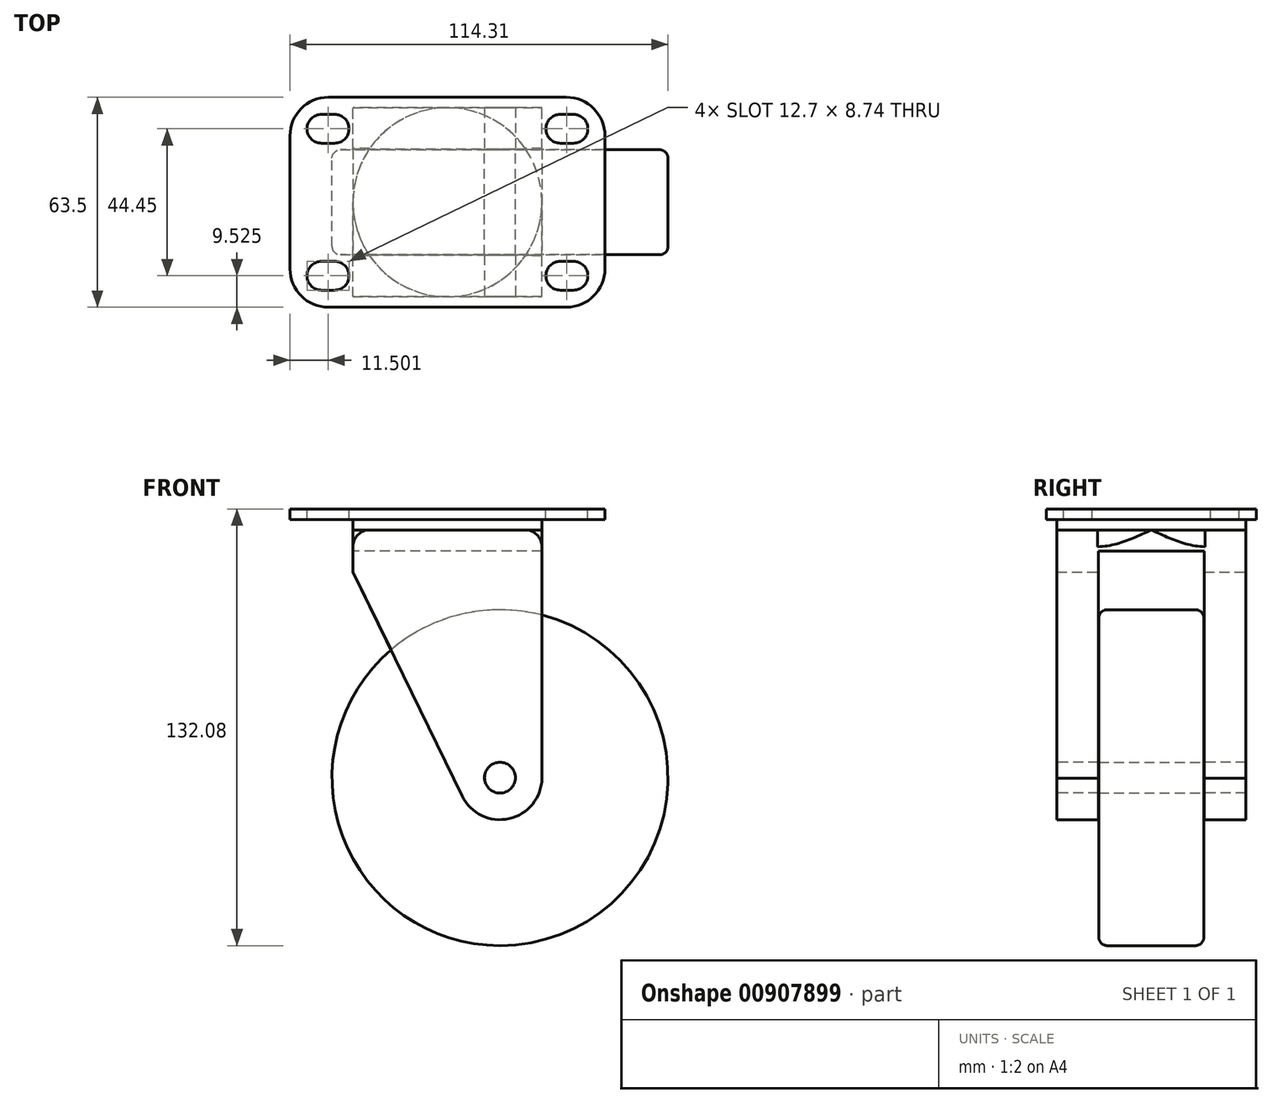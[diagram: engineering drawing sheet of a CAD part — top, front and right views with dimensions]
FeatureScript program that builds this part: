
annotation { "Feature Type Name" : "Feature", "Feature Type Description" : "" }
export const myFeature = defineFeature(function(context is Context, id is Id, definition is map)
    precondition{}
    {
        {
            var Q0;
            Q0=qCreatedBy(makeId("Top.planeOp"),FACE);
            var sketch = newSketch(context, id + "F0", { "sketchPlane" : qUnion([Q0])});
            skLineSegment(sketch, "E0.bottom", {"start": v(-47.62, 31.75) * mm, "end": v(47.63, 31.75) * mm});
            skLineSegment(sketch, "E0.top", {"start": v(-47.62, -31.75) * mm, "end": v(47.63, -31.75) * mm});
            skLineSegment(sketch, "E0.left", {"start": v(-47.62, 31.75) * mm, "end": v(-47.63, -31.75) * mm});
            skLineSegment(sketch, "E0.right", {"start": v(47.63, 31.75) * mm, "end": v(47.62, -31.75) * mm});
            skPoint(sketch, "E0.middle", {"position": v(0, 0) * mm});
            skArc(sketch, "E1", {"start": v(-38.1, -17.86) * mm, "mid": v(-42.47, -22.23) * mm, "end": v(-38.1, -26.6) * mm});
            skArc(sketch, "E2", {"start": v(-34.14, -26.6) * mm, "mid": v(-29.77, -22.23) * mm, "end": v(-34.14, -17.86) * mm});
            skLineSegment(sketch, "E3", {"start": v(-38.1, -26.6) * mm, "end": v(-34.14, -26.6) * mm});
            skLineSegment(sketch, "E4", {"start": v(-34.14, -17.86) * mm, "end": v(-38.1, -17.86) * mm});
            skArc(sketch, "E5.MirrorCS", {"start": v(-38.1, 17.86) * mm, "mid": v(-42.47, 22.23) * mm, "end": v(-38.1, 26.6) * mm});
            skLineSegment(sketch, "E6.MirrorCS", {"start": v(-34.14, 17.86) * mm, "end": v(-38.1, 17.86) * mm});
            skLineSegment(sketch, "E7.MirrorCS", {"start": v(-38.1, 26.6) * mm, "end": v(-34.14, 26.6) * mm});
            skArc(sketch, "E8.MirrorCS", {"start": v(-34.14, 26.6) * mm, "mid": v(-29.77, 22.23) * mm, "end": v(-34.14, 17.86) * mm});
            skLineSegment(sketch, "E9.MirrorCS", {"start": v(34.14, -17.86) * mm, "end": v(38.1, -17.86) * mm});
            skLineSegment(sketch, "E10.MirrorCS", {"start": v(38.1, -26.6) * mm, "end": v(34.14, -26.6) * mm});
            skArc(sketch, "E11.MirrorCS", {"start": v(34.14, -26.6) * mm, "mid": v(29.77, -22.23) * mm, "end": v(34.14, -17.86) * mm});
            skLineSegment(sketch, "E12.MirrorCS", {"start": v(38.1, 26.6) * mm, "end": v(34.14, 26.6) * mm});
            skLineSegment(sketch, "E13.MirrorCS", {"start": v(34.14, 17.86) * mm, "end": v(38.1, 17.86) * mm});
            skArc(sketch, "E14.MirrorCS", {"start": v(34.14, 26.6) * mm, "mid": v(29.77, 22.23) * mm, "end": v(34.14, 17.86) * mm});
            skLineSegment(sketch, "E15.MirrorCS", {"start": v(47.62, 31.75) * mm, "end": v(47.63, -31.75) * mm});
            skLineSegment(sketch, "E16.MirrorCS", {"start": v(47.62, -31.75) * mm, "end": v(-47.63, -31.75) * mm});
            skArc(sketch, "E17.MirrorCS", {"start": v(38.1, -17.86) * mm, "mid": v(42.47, -22.23) * mm, "end": v(38.1, -26.6) * mm});
            skLineSegment(sketch, "E18.MirrorCS", {"start": v(47.62, 31.75) * mm, "end": v(-47.63, 31.75) * mm});
            skArc(sketch, "E19.MirrorCS", {"start": v(38.1, 17.86) * mm, "mid": v(42.47, 22.23) * mm, "end": v(38.1, 26.6) * mm});
            skSolve(sketch);
        }
        {
            var Q0;
            Q0=makeQuery(id+"F0.imprint","IMPRINT",FACE,{"disambiguationData":[TD([[makeQuery(id+"F0.imprint","IMPRINT",EDGE,{"derivedFrom":sQuery(id+"F0.wireOp",EDGE,"E0.left")}),1.0]])]});
            extrude(context, id + "F1", {"entities" : qUnion([Q0]), "oppositeDirection" : true, "depth" : 3.17 * mm, "offsetDistance" : 25.4 * mm});
        }
        {
            var Q0;
            Q0=makeQuery(id+"F1.opExtrude","CAP_FACE",FACE,{"disambiguationData":[OSD([sQuery(id+"F0.wireOp",EDGE,"E0.left"),sQuery(id+"F0.wireOp",EDGE,"E1"),sQuery(id+"F0.wireOp",EDGE,"E2"),sQuery(id+"F0.wireOp",EDGE,"E3"),sQuery(id+"F0.wireOp",EDGE,"E4"),sQuery(id+"F0.wireOp",EDGE,"E5.MirrorCS"),sQuery(id+"F0.wireOp",EDGE,"E6.MirrorCS"),sQuery(id+"F0.wireOp",EDGE,"E7.MirrorCS"),sQuery(id+"F0.wireOp",EDGE,"E8.MirrorCS"),sQuery(id+"F0.wireOp",EDGE,"E10.MirrorCS"),sQuery(id+"F0.wireOp",EDGE,"E9.MirrorCS"),sQuery(id+"F0.wireOp",EDGE,"E12.MirrorCS"),sQuery(id+"F0.wireOp",EDGE,"E13.MirrorCS"),sQuery(id+"F0.wireOp",EDGE,"E11.MirrorCS"),sQuery(id+"F0.wireOp",EDGE,"E14.MirrorCS"),sQuery(id+"F0.wireOp",EDGE,"E15.MirrorCS"),sQuery(id+"F0.wireOp",EDGE,"E16.MirrorCS"),sQuery(id+"F0.wireOp",EDGE,"E17.MirrorCS"),sQuery(id+"F0.wireOp",EDGE,"E18.MirrorCS"),sQuery(id+"F0.wireOp",EDGE,"E19.MirrorCS")])],"isStart":false});
            var sketch = newSketch(context, id + "F2", { "sketchPlane" : qUnion([Q0])});
            skCircle(sketch, "E20", {"center": v(0, 0) * mm, "radius": 28.57 * mm});
            skSolve(sketch);
        }
        {
            var Q0;
            Q0=makeQuery(id+"F2.imprint","IMPRINT",FACE,{"disambiguationData":[TD([[makeQuery(id+"F2.imprint","IMPRINT",EDGE,{"derivedFrom":sQuery(id+"F2.wireOp",EDGE,"E20")}),1.0]])]});
            extrude(context, id + "F3", {"entities" : qUnion([Q0]), "operationType" : NewBodyOperationType.ADD, "depth" : 3.17 * mm, "offsetDistance" : 25.4 * mm});
        }
        {
            var Q0;
            Q0=qCreatedBy(makeId("Front.planeOp"),FACE);
            var sketch = newSketch(context, id + "F4", { "sketchPlane" : qUnion([Q0])});
            skLineSegment(sketch, "E21.bottom", {"start": v(28.58, -6.35) * mm, "end": v(-28.57, -6.35) * mm});
            skLineSegment(sketch, "E21.top", {"start": v(28.58, -19.05) * mm, "end": v(-28.57, -19.05) * mm});
            skLineSegment(sketch, "E21.left", {"start": v(28.58, -6.35) * mm, "end": v(28.58, -19.05) * mm});
            skLineSegment(sketch, "E21.right", {"start": v(-28.57, -6.35) * mm, "end": v(-28.57, -19.05) * mm});
            skArc(sketch, "E22", {"start": v(4.46, -86.84) * mm, "mid": v(18.83, -93.63) * mm, "end": v(28.57, -81.07) * mm});
            skLineSegment(sketch, "E23", {"start": v(28.57, -81.49) * mm, "end": v(28.58, -19.05) * mm});
            skLineSegment(sketch, "E24", {"start": v(-28.58, -19.05) * mm, "end": v(4.46, -86.84) * mm});
            skSolve(sketch);
        }
        {
            var Q0;
            {var subQ1=sQuery(id+"F4.wireOp",EDGE,"E21.top");Q0=makeQuery(id+"F4.imprint","IMPRINT",FACE,{"disambiguationData":[TD([[makeQuery(id+"F4.imprint","IMPRINT",EDGE,{"derivedFrom":subQ1}),1.0]])]});}
            var Q1;
            Q1=makeQuery(id+"F4.imprint","IMPRINT",FACE,{"disambiguationData":[TD([[makeQuery(id+"F4.imprint","IMPRINT",EDGE,{"derivedFrom":sQuery(id+"F4.wireOp",EDGE,"E21.bottom")}),1.0]])]});
            extrude(context, id + "F5", {"entities" : qUnion([Q0, Q1]), "operationType" : NewBodyOperationType.ADD, "depth" : 28.57 * mm, "offsetDistance" : 25.4 * mm, "hasSecondDirection" : true, "secondDirectionOppositeDirection" : true, "secondDirectionDepth" : 28.57 * mm});
        }
        {
            var Q0;
            Q0=qCreatedBy(makeId("Right.planeOp"),FACE);
            var sketch = newSketch(context, id + "F6", { "sketchPlane" : qUnion([Q0])});
            skLineSegment(sketch, "E25.bottom", {"start": v(-16, -125.42) * mm, "end": v(16, -125.42) * mm});
            skLineSegment(sketch, "E25.top", {"start": v(-16, -12.7) * mm, "end": v(16, -12.7) * mm});
            skLineSegment(sketch, "E25.left", {"start": v(-16, -125.42) * mm, "end": v(-16, -12.7) * mm});
            skLineSegment(sketch, "E25.right", {"start": v(16, -125.42) * mm, "end": v(16, -12.7) * mm});
            skSolve(sketch);
        }
        {
            var Q0;
            Q0 = qSketchRegion(id + "F6", true);
            extrude(context, id + "F7", {"entities" : qUnion([Q0]), "operationType" : NewBodyOperationType.REMOVE, "depth" : 50.8 * mm, "offsetDistance" : 25.4 * mm, "hasSecondDirection" : true, "secondDirectionOppositeDirection" : true, "secondDirectionDepth" : 50.8 * mm});
        }
        {
            var Q0;
            Q0=makeQuery(id+"F5.opExtrude","CAP_FACE",FACE,{"disambiguationData":[OSD([sQuery(id+"F4.wireOp",EDGE,"E21.bottom"),sQuery(id+"F4.wireOp",EDGE,"E21.left"),sQuery(id+"F4.wireOp",EDGE,"E21.right"),sQuery(id+"F4.wireOp",EDGE,"E22"),sQuery(id+"F4.wireOp",EDGE,"E23"),sQuery(id+"F4.wireOp",EDGE,"E24")])],"isStart":false});
            var sketch = newSketch(context, id + "F8", { "sketchPlane" : qUnion([Q0])});
            skPoint(sketch, "E26", {"position": v(15.88, -81.28) * mm});
            skSolve(sketch);
        }
        {
            var Q0;
            Q0=sQuery(id+"F8.wireOp",VERTEX,"E26");
            var Q1;
            Q1=makeQuery(id+"F1.opExtrude","SWEPT_BODY",BODY,{"disambiguationData":[OSD([sQuery(id+"F0.wireOp",EDGE,"E0.left"),sQuery(id+"F0.wireOp",EDGE,"E1"),sQuery(id+"F0.wireOp",EDGE,"E2"),sQuery(id+"F0.wireOp",EDGE,"E3"),sQuery(id+"F0.wireOp",EDGE,"E4"),sQuery(id+"F0.wireOp",EDGE,"E5.MirrorCS"),sQuery(id+"F0.wireOp",EDGE,"E6.MirrorCS"),sQuery(id+"F0.wireOp",EDGE,"E7.MirrorCS"),sQuery(id+"F0.wireOp",EDGE,"E8.MirrorCS"),sQuery(id+"F0.wireOp",EDGE,"E10.MirrorCS"),sQuery(id+"F0.wireOp",EDGE,"E9.MirrorCS"),sQuery(id+"F0.wireOp",EDGE,"E12.MirrorCS"),sQuery(id+"F0.wireOp",EDGE,"E13.MirrorCS"),sQuery(id+"F0.wireOp",EDGE,"E11.MirrorCS"),sQuery(id+"F0.wireOp",EDGE,"E14.MirrorCS"),sQuery(id+"F0.wireOp",EDGE,"E15.MirrorCS"),sQuery(id+"F0.wireOp",EDGE,"E16.MirrorCS"),sQuery(id+"F0.wireOp",EDGE,"E17.MirrorCS"),sQuery(id+"F0.wireOp",EDGE,"E18.MirrorCS"),sQuery(id+"F0.wireOp",EDGE,"E19.MirrorCS")])]});
            hole(context, id + "F9", {"style" : HoleStyle.SIMPLE, "endStyle" : HoleEndStyle.THROUGH, "standardTappedOrClearance" : lookupTablePath({ "standard" : "ANSI", "engagement" : "75%", "pitch" : "14 tpi", "size" : "7/16", "type" : "Tapped" }), "standardBlindInLast" : lookupTablePath({ "standard" : "ANSI", "engagement" : "75%", "pitch" : "14 tpi", "size" : "7/16", "type" : "Tapped" }), "holeDiameter" : 9.35 * mm, "majorDiameter" : 11.1 * mm, "showTappedDepth" : true, "isTappedThrough" : true, "tappedDepth" : 12.71 * mm, "tapClearance" : 3, "startFromSketch" : true, "locations" : qUnion([Q0]), "scope" : qUnion([Q1])});
        }
        {
            var Q0;
            {var subQ0=sQuery(id+"F4.wireOp",EDGE,"E21.bottom");var subQ1=sQuery(id+"F4.wireOp",EDGE,"E21.right");Q0=makeQuery(id+"F5.boolean.opBoolean","SPLIT",EDGE,{"disambiguationData":[TD([makeQuery(id+"F5.opExtrude","CAP_FACE",FACE,{"disambiguationData":[OSD([subQ0,sQuery(id+"F4.wireOp",EDGE,"E21.left"),subQ1,sQuery(id+"F4.wireOp",EDGE,"E22"),sQuery(id+"F4.wireOp",EDGE,"E23"),sQuery(id+"F4.wireOp",EDGE,"E24")])],"isStart":false})])],"derivedFrom":makeQuery(id+"F5.opExtrude","SWEPT_EDGE",EDGE,{"disambiguationData":[OSD([subQ0,subQ1])]})});}
            var Q1;
            {var subQ0=sQuery(id+"F4.wireOp",EDGE,"E21.bottom");var subQ1=sQuery(id+"F4.wireOp",EDGE,"E21.left");Q1=makeQuery(id+"F5.boolean.opBoolean","SPLIT",EDGE,{"disambiguationData":[TD([makeQuery(id+"F5.opExtrude","CAP_FACE",FACE,{"disambiguationData":[OSD([subQ0,subQ1,sQuery(id+"F4.wireOp",EDGE,"E21.right"),sQuery(id+"F4.wireOp",EDGE,"E22"),sQuery(id+"F4.wireOp",EDGE,"E23"),sQuery(id+"F4.wireOp",EDGE,"E24")])],"isStart":false})])],"derivedFrom":makeQuery(id+"F5.opExtrude","SWEPT_EDGE",EDGE,{"disambiguationData":[OSD([subQ0,subQ1])]})});}
            fillet(context, id + "F10", {"entities" : qUnion([Q0, Q1]), "radius" : 5.08 * mm, "tangentPropagation" : true, "allowEdgeOverflow" : false});
        }
        {
            var Q0;
            Q0=makeQuery(id+"F1.opExtrude","SWEPT_EDGE",EDGE,{"disambiguationData":[OSD([sQuery(id+"F0.wireOp",EDGE,"E15.MirrorCS"),sQuery(id+"F0.wireOp",EDGE,"E16.MirrorCS")])]});
            var Q1;
            Q1=makeQuery(id+"F1.opExtrude","SWEPT_EDGE",EDGE,{"disambiguationData":[OSD([sQuery(id+"F0.wireOp",EDGE,"E15.MirrorCS"),sQuery(id+"F0.wireOp",EDGE,"E18.MirrorCS")])]});
            var Q2;
            Q2=makeQuery(id+"F1.opExtrude","SWEPT_EDGE",EDGE,{"disambiguationData":[OSD([sQuery(id+"F0.wireOp",EDGE,"E0.left"),sQuery(id+"F0.wireOp",EDGE,"E18.MirrorCS")])]});
            var Q3;
            Q3=makeQuery(id+"F1.opExtrude","SWEPT_EDGE",EDGE,{"disambiguationData":[OSD([sQuery(id+"F0.wireOp",EDGE,"E0.left"),sQuery(id+"F0.wireOp",EDGE,"E16.MirrorCS")])]});
            fillet(context, id + "F11", {"entities" : qUnion([Q0, Q1, Q2, Q3]), "radius" : 11.65 * mm, "tangentPropagation" : true, "allowEdgeOverflow" : false});
        }
        {
            var Q0;
            Q0=qCreatedBy(makeId("Front.planeOp"),FACE);
            var sketch = newSketch(context, id + "F12", { "sketchPlane" : qUnion([Q0])});
            skCircle(sketch, "E27", {"center": v(15.89, -81.28) * mm, "radius": 50.8 * mm});
            skCircle(sketch, "E28", {"center": v(15.89, -81.28) * mm, "radius": 4.67 * mm});
            skSolve(sketch);
        }
        {
            var Q0;
            Q0=makeQuery(id+"F12.imprint","IMPRINT",FACE,{"disambiguationData":[TD([[makeQuery(id+"F12.imprint","IMPRINT",EDGE,{"derivedFrom":sQuery(id+"F12.wireOp",EDGE,"E27")}),1.0]])]});
            extrude(context, id + "F13", {"entities" : qUnion([Q0]), "depth" : 15.88 * mm, "offsetDistance" : 25.4 * mm, "hasSecondDirection" : true, "secondDirectionOppositeDirection" : true, "secondDirectionDepth" : 15.88 * mm});
        }
        {
            var Q0;
            Q0=makeQuery(id+"F13.opExtrude","CAP_EDGE",EDGE,{"disambiguationData":[OSD([sQuery(id+"F12.wireOp",EDGE,"E27")])],"isStart":false});
            var Q1;
            Q1=makeQuery(id+"F13.opExtrude","CAP_EDGE",EDGE,{"disambiguationData":[OSD([sQuery(id+"F12.wireOp",EDGE,"E27")])],"isStart":true});
            fillet(context, id + "F14", {"entities" : qUnion([Q0, Q1]), "radius" : 2.54 * mm, "tangentPropagation" : true, "allowEdgeOverflow" : false});
        }
    });
